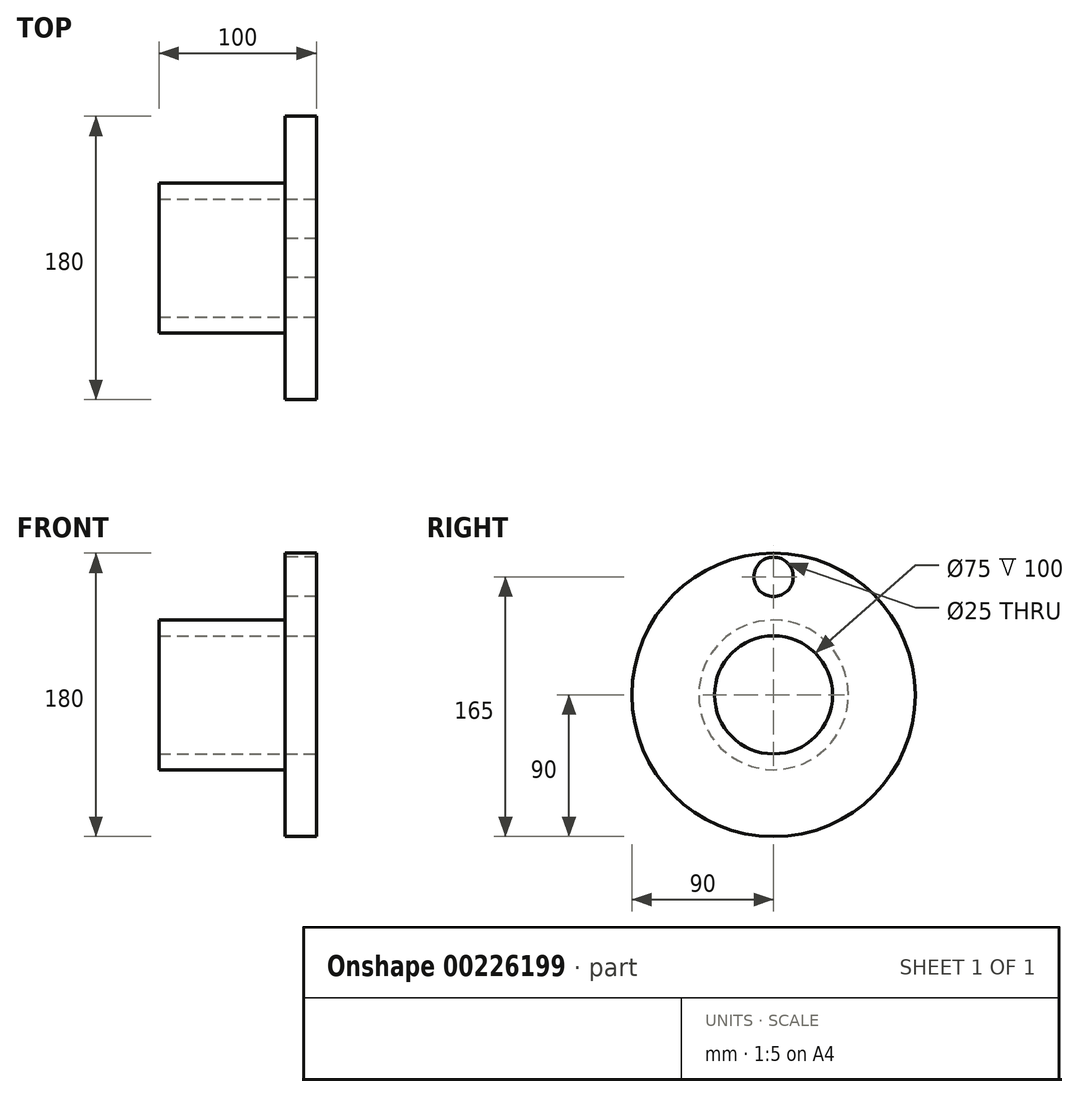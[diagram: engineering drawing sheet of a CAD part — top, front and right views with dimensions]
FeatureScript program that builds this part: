
annotation { "Feature Type Name" : "Feature", "Feature Type Description" : "" }
export const myFeature = defineFeature(function(context is Context, id is Id, definition is map)
    precondition{}
    {
        {
            var Q0;
            Q0=qCreatedBy(makeId("Front.planeOp"),FACE);
            var sketch = newSketch(context, id + "F0", { "sketchPlane" : qUnion([Q0])});
            skLineSegment(sketch, "E0", {"start": v(0, 0) * mm, "end": v(-181.48, 0) * mm, "construction": true});
            skLineSegment(sketch, "E1.bottom", {"start": v(0, 37.5) * mm, "end": v(-100, 37.5) * mm});
            skLineSegment(sketch, "E1.top", {"start": v(0, 90) * mm, "end": v(-20, 90) * mm});
            skLineSegment(sketch, "E1.left", {"start": v(0, 37.5) * mm, "end": v(0, 90) * mm});
            skLineSegment(sketch, "E1.right", {"start": v(-100, 37.5) * mm, "end": v(-100, 47.5) * mm});
            skLineSegment(sketch, "E2.top", {"start": v(-100, 47.5) * mm, "end": v(-20, 47.5) * mm});
            skLineSegment(sketch, "E2.right", {"start": v(-20, 90) * mm, "end": v(-20, 47.5) * mm});
            skSolve(sketch);
        }
        {
            var Q0;
            Q0 = qSketchRegion(id + "F0", true);
            var Q1;
            Q1=sQuery(id+"F0.wireOp",EDGE,"E0");
            revolve(context, id + "F1", {"entities" : qUnion([Q0]), "axis" : qUnion([Q1]), "revolveType" : RevolveType.FULL});
        }
        {
            var Q0;
            Q0=makeQuery(id+"F1.opRevolve","SWEPT_FACE",FACE,{"disambiguationData":[OSD([sQuery(id+"F0.wireOp",EDGE,"E2.right")])]});
            var sketch = newSketch(context, id + "F2", { "sketchPlane" : qUnion([Q0])});
            skCircle(sketch, "E3", {"center": v(0, 75) * mm, "radius": 12.5 * mm});
            skSolve(sketch);
        }
        {
            var Q0;
            Q0=makeQuery(id+"F2.imprint","IMPRINT",FACE,{"disambiguationData":[TD([[makeQuery(id+"F2.imprint","IMPRINT",EDGE,{"derivedFrom":sQuery(id+"F2.wireOp",EDGE,"E3")}),1.0]])]});
            extrude(context, id + "F3", {"entities" : qUnion([Q0]), "operationType" : NewBodyOperationType.REMOVE, "endBound" : BoundingType.THROUGH_ALL, "oppositeDirection" : true, "depth" : 25 * mm});
        }
    });
